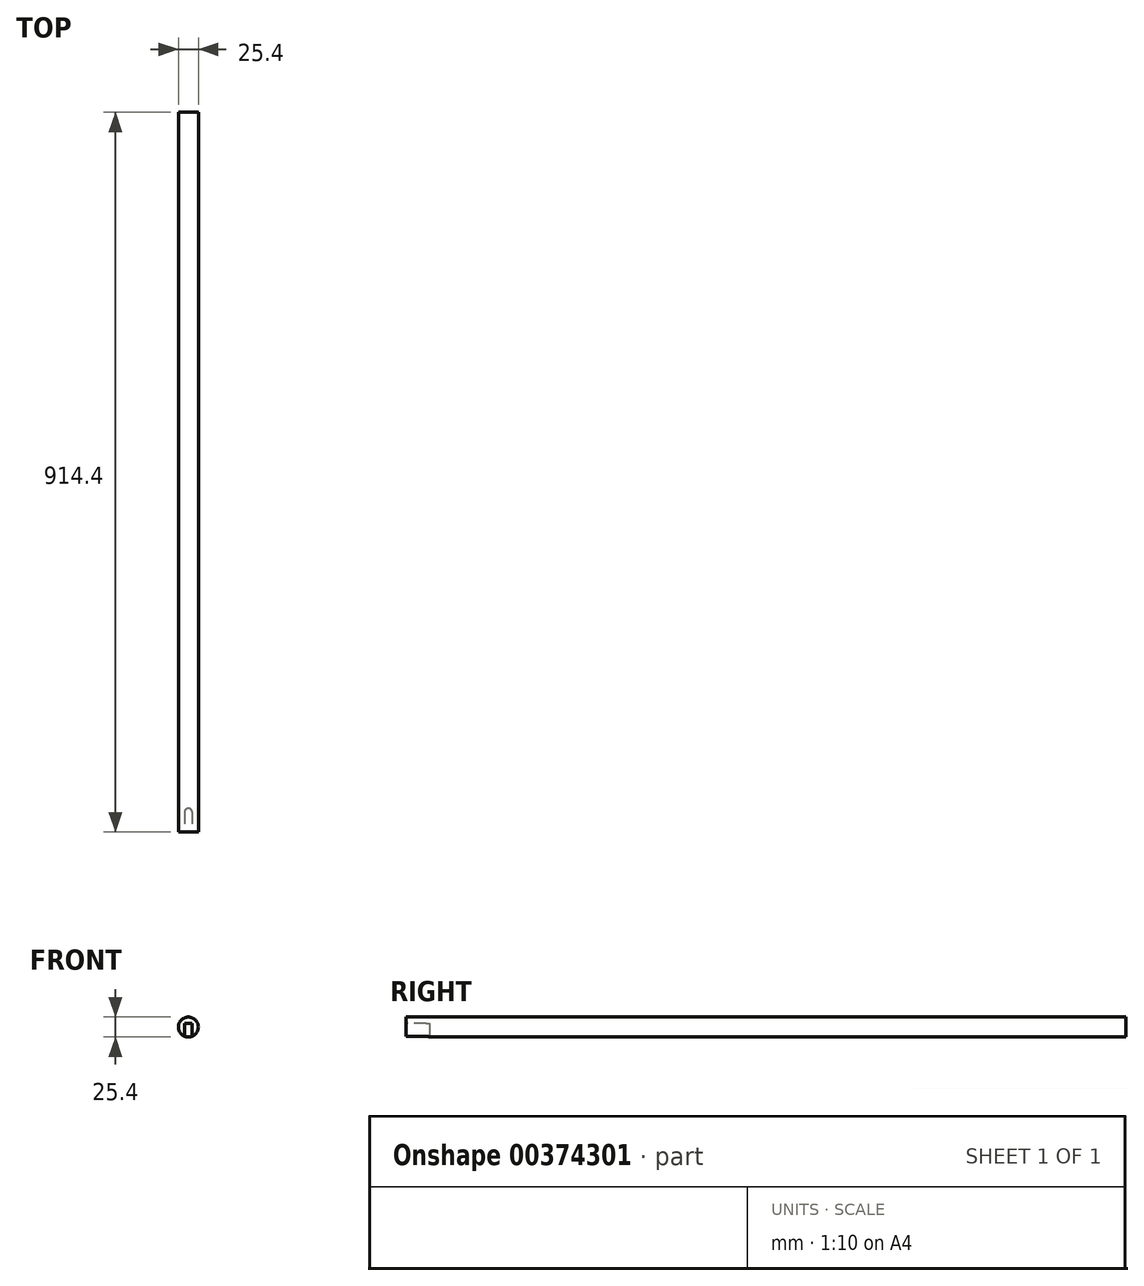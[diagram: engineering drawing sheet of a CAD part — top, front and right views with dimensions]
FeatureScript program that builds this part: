
annotation { "Feature Type Name" : "Feature", "Feature Type Description" : "" }
export const myFeature = defineFeature(function(context is Context, id is Id, definition is map)
    precondition{}
    {
        {
            var Q0;
            Q0=qCreatedBy(makeId("Front.planeOp"),FACE);
            var sketch = newSketch(context, id + "F0", { "sketchPlane" : qUnion([Q0])});
            skCircle(sketch, "E0", {"center": v(0, 0) * mm, "radius": 12.7 * mm});
            skSolve(sketch);
        }
        {
            var Q0;
            Q0=makeQuery(id+"F0.imprint","IMPRINT",FACE,{"disambiguationData":[TD([[makeQuery(id+"F0.imprint","IMPRINT",EDGE,{"derivedFrom":sQuery(id+"F0.wireOp",EDGE,"E0")}),1.0]])]});
            extrude(context, id + "F1", {"entities" : qUnion([Q0]), "oppositeDirection" : true, "depth" : 914.4 * mm});
        }
        {
            var Q0;
            Q0=makeQuery(id+"F1.opExtrude","CAP_FACE",FACE,{"disambiguationData":[OSD([sQuery(id+"F0.wireOp",EDGE,"E0")])],"isStart":true});
            var sketch = newSketch(context, id + "F2", { "sketchPlane" : qUnion([Q0])});
            skLineSegment(sketch, "E1.bottom", {"start": v(-4.76, 4.76) * mm, "end": v(4.76, 4.76) * mm});
            skLineSegment(sketch, "E1.left", {"start": v(-4.76, 4.76) * mm, "end": v(-4.76, -11.77) * mm});
            skLineSegment(sketch, "E1.right", {"start": v(4.76, 4.76) * mm, "end": v(4.76, -11.77) * mm});
            skCircle(sketch, "E2.0.0", {"center": v(0, 0) * mm, "radius": 12.7 * mm});
            skSolve(sketch);
        }
        {
            var Q0;
            Q0=makeQuery(id+"F2.imprint","IMPRINT",FACE,{"disambiguationData":[TD([[makeQuery(id+"F2.imprint","IMPRINT",EDGE,{"derivedFrom":sQuery(id+"F2.wireOp",EDGE,"E1.bottom")}),-1.0]])]});
            extrude(context, id + "F3", {"entities" : qUnion([Q0]), "operationType" : NewBodyOperationType.REMOVE, "oppositeDirection" : true, "depth" : 25.4 * mm});
        }
        {
            var Q0;
            Q0=qCreatedBy(makeId("Top.planeOp"),FACE);
            cPlane(context, id + "F4", {"entities" : qUnion([Q0]), "cplaneType" : CPlaneType.OFFSET, "offset" : 12.7 * mm, "oppositeDirection" : true, "width" : 152.4 * mm, "height" : 152.4 * mm});
        }
        {
            var Q0;
            Q0=qCreatedBy(id+"F4.planeOp",FACE);
            var sketch = newSketch(context, id + "F5", { "sketchPlane" : qUnion([Q0])});
            skLineSegment(sketch, "E3.0", {"start": v(-4.76, 25.4) * mm, "end": v(4.76, 25.4) * mm});
            skCircle(sketch, "E4", {"center": v(0, 25.4) * mm, "radius": 4.76 * mm});
            skSolve(sketch);
        }
        {
            var Q0;
            {var subQ0=sQuery(id+"F5.wireOp",EDGE,"E3.0");Q0=makeQuery(id+"F5.imprint","IMPRINT",FACE,{"disambiguationData":[TD([[makeQuery(id+"F5.imprint","IMPRINT",EDGE,{"derivedFrom":subQ0}),1.0]])]});}
            var Q1;
            Q1=makeQuery(id+"F3.boolean.opBoolean","COPY",FACE,{"derivedFrom":makeQuery(id+"F3.opExtrude","SWEPT_FACE",FACE,{"disambiguationData":[OSD([sQuery(id+"F2.wireOp",EDGE,"E1.bottom")])]})});
            extrude(context, id + "F6", {"entities" : qUnion([Q0]), "operationType" : NewBodyOperationType.REMOVE, "endBound" : BoundingType.UP_TO_SURFACE, "endBoundEntityFace" : qUnion([Q1]), "depth" : 12.7 * mm});
        }
    });
